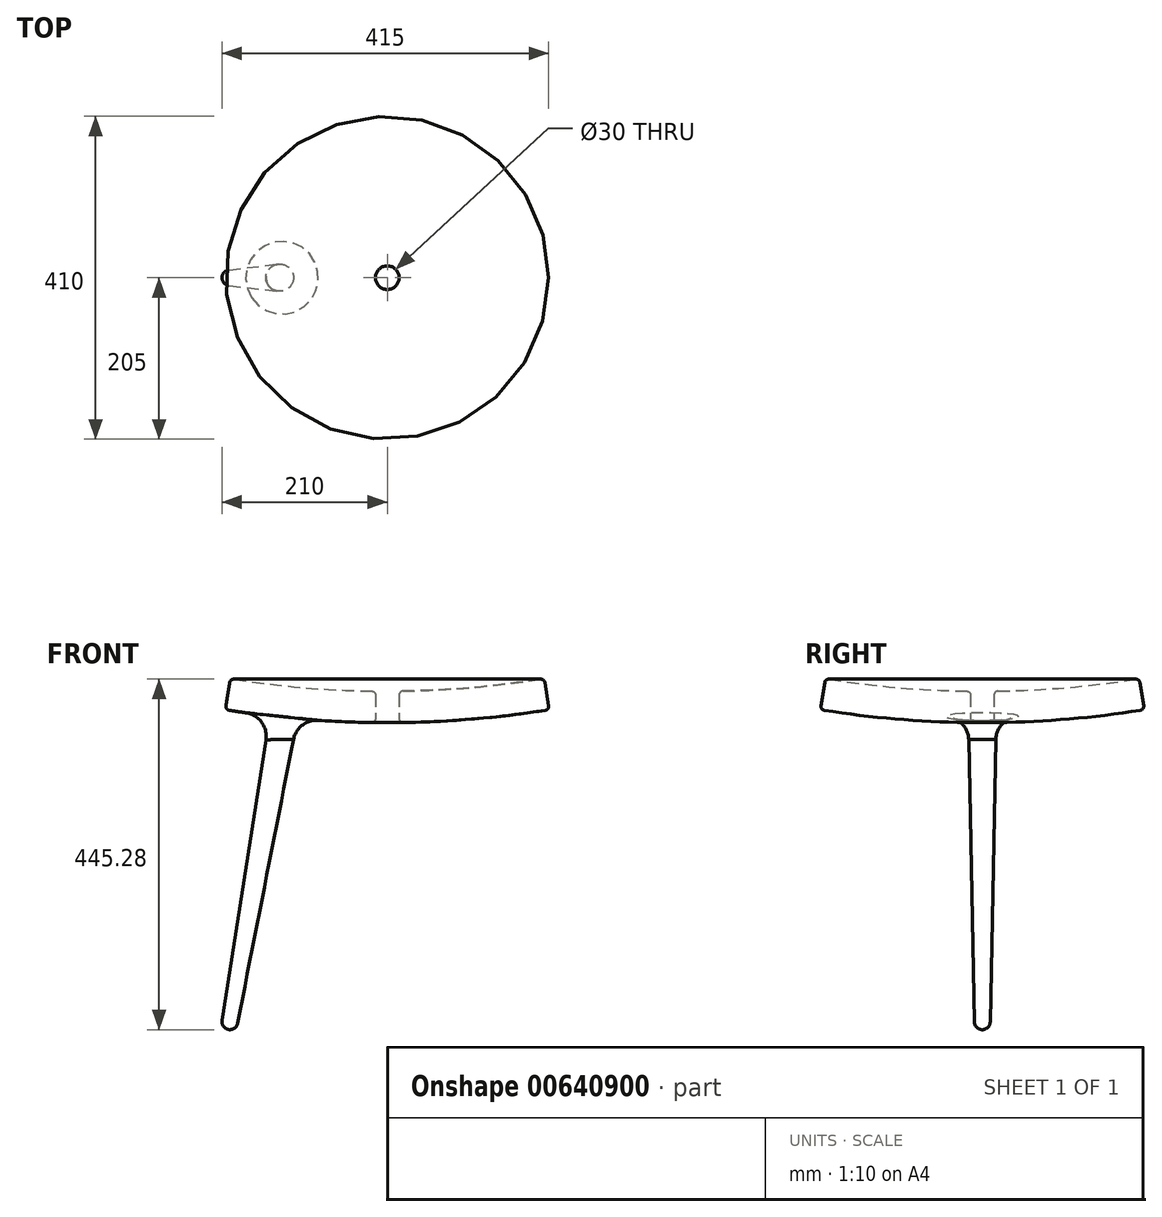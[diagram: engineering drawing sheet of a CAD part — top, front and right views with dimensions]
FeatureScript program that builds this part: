
annotation { "Feature Type Name" : "Feature", "Feature Type Description" : "" }
export const myFeature = defineFeature(function(context is Context, id is Id, definition is map)
    precondition{}
    {
        {
            var Q0;
            Q0=qCreatedBy(makeId("Front.planeOp"),FACE);
            var sketch = newSketch(context, id + "F0", { "sketchPlane" : qUnion([Q0])});
            skArc(sketch, "E0", {"start": v(0, 430) * mm, "mid": v(100, 434) * mm, "end": v(199.36, 446) * mm});
            skLineSegment(sketch, "E1", {"start": v(0, 0) * mm, "end": v(0, 1680) * mm, "construction": true});
            skLineSegment(sketch, "E2", {"start": v(199.36, 446) * mm, "end": v(205.74, 406.51) * mm});
            skArc(sketch, "E3.0", {"start": v(0, 390) * mm, "mid": v(103.2, 394.13) * mm, "end": v(205.74, 406.51) * mm});
            skLineSegment(sketch, "E4", {"start": v(0, 430) * mm, "end": v(0, 390) * mm});
            skSolve(sketch);
        }
        {
            var Q0;
            Q0=makeQuery(id+"F0.imprint","IMPRINT",FACE,{"disambiguationData":[TD([[makeQuery(id+"F0.imprint","IMPRINT",EDGE,{"derivedFrom":sQuery(id+"F0.wireOp",EDGE,"E0")}),-1.0]])]});
            var Q1;
            Q1=sQuery(id+"F0.wireOp",EDGE,"E1");
            revolve(context, id + "F1", {"entities" : qUnion([Q0]), "axis" : qUnion([Q1]), "revolveType" : RevolveType.FULL});
        }
        {
            var Q0;
            Q0=qCreatedBy(makeId("Front.planeOp"),FACE);
            var sketch = newSketch(context, id + "F2", { "sketchPlane" : qUnion([Q0])});
            skLineSegment(sketch, "E5", {"start": v(0, 0) * mm, "end": v(-318.45, 0) * mm, "construction": true});
            skArc(sketch, "E6", {"start": v(-201.74, 0.15) * mm, "mid": v(-194.35, 1.75) * mm, "end": v(-190.19, 8.07) * mm});
            skLineSegment(sketch, "E7", {"start": v(-201.74, 0.15) * mm, "end": v(-130.54, 403.92) * mm});
            skPoint(sketch, "E8.orphan", {"position": v(0, 0) * mm});
            skLineSegment(sketch, "E9", {"start": v(-130.54, 403.92) * mm, "end": v(-112.81, 400.8) * mm});
            skLineSegment(sketch, "E10", {"start": v(-112.81, 400.8) * mm, "end": v(-190.19, 8.07) * mm});
            skSolve(sketch);
        }
        {
            var Q0;
            Q0=qCreatedBy(makeId("Front.planeOp"),FACE);
            var sketch = newSketch(context, id + "F3", { "sketchPlane" : qUnion([Q0])});
            skLineSegment(sketch, "E11", {"start": v(0, 0) * mm, "end": v(0, 234.57) * mm, "construction": true});
            skSolve(sketch);
        }
        {
            var Q0;
            Q0=makeQuery(id+"F2.imprint","IMPRINT",FACE,{"disambiguationData":[TD([[makeQuery(id+"F2.imprint","IMPRINT",EDGE,{"derivedFrom":sQuery(id+"F2.wireOp",EDGE,"E6")}),1.0]])]});
            var Q1;
            Q1=sQuery(id+"F2.wireOp",EDGE,"E7");
            revolve(context, id + "F4", {"operationType" : NewBodyOperationType.ADD, "entities" : qUnion([Q0]), "axis" : qUnion([Q1]), "revolveType" : RevolveType.FULL});
        }
        {
            var Q0;
            Q0=makeQuery(id+"Fkk3XBELj9BTLDk_1.1.F4.boolean.opBoolean","INTERSECT",EDGE,{"derivedFrom":[makeQuery(id+"F1.opRevolve","SWEPT_FACE",FACE,{"disambiguationData":[OSD([sQuery(id+"F0.wireOp",EDGE,"E3.0")])]}),makeQuery(id+"Fkk3XBELj9BTLDk_1.1.F4.opRevolve","SWEPT_FACE",FACE,{"disambiguationData":[OSD([sQuery(id+"F2.wireOp",EDGE,"E10")])]})]});
            var Q1;
            Q1=makeQuery(id+"Fkk3XBELj9BTLDk_1.2.F4.boolean.opBoolean","INTERSECT",EDGE,{"derivedFrom":[makeQuery(id+"F1.opRevolve","SWEPT_FACE",FACE,{"disambiguationData":[OSD([sQuery(id+"F0.wireOp",EDGE,"E3.0")])]}),makeQuery(id+"Fkk3XBELj9BTLDk_1.2.F4.opRevolve","SWEPT_FACE",FACE,{"disambiguationData":[OSD([sQuery(id+"F2.wireOp",EDGE,"E10")])]})]});
            var Q2;
            Q2=makeQuery(id+"Fkk3XBELj9BTLDk_1.3.F4.boolean.opBoolean","INTERSECT",EDGE,{"derivedFrom":[makeQuery(id+"F1.opRevolve","SWEPT_FACE",FACE,{"disambiguationData":[OSD([sQuery(id+"F0.wireOp",EDGE,"E3.0")])]}),makeQuery(id+"Fkk3XBELj9BTLDk_1.3.F4.opRevolve","SWEPT_FACE",FACE,{"disambiguationData":[OSD([sQuery(id+"F2.wireOp",EDGE,"E10")])]})]});
            var Q3;
            Q3=makeQuery(id+"F4.boolean.opBoolean","INTERSECT",EDGE,{"derivedFrom":[makeQuery(id+"F1.opRevolve","SWEPT_FACE",FACE,{"disambiguationData":[OSD([sQuery(id+"F0.wireOp",EDGE,"E3.0")])]}),makeQuery(id+"F4.opRevolve","SWEPT_FACE",FACE,{"disambiguationData":[OSD([sQuery(id+"F2.wireOp",EDGE,"E10")])]})]});
            fillet(context, id + "F5", {"entities" : qUnion([Q0, Q1, Q2, Q3]), "radius" : 30 * mm, "tangentPropagation" : true, "allowEdgeOverflow" : false});
        }
        {
            var Q0;
            Q0=makeQuery(id+"F1.opRevolve","SWEPT_EDGE",EDGE,{"disambiguationData":[OSD([sQuery(id+"F0.wireOp",EDGE,"E0"),sQuery(id+"F0.wireOp",EDGE,"E2")])]});
            var Q1;
            Q1=makeQuery(id+"F1.opRevolve","SWEPT_EDGE",EDGE,{"disambiguationData":[OSD([sQuery(id+"F0.wireOp",EDGE,"E2"),sQuery(id+"F0.wireOp",EDGE,"E3.0")])]});
            fillet(context, id + "F6", {"entities" : qUnion([Q0, Q1]), "radius" : 5 * mm, "tangentPropagation" : true, "allowEdgeOverflow" : false});
        }
        {
            var Q0;
            Q0=qCreatedBy(makeId("Top.planeOp"),FACE);
            var sketch = newSketch(context, id + "F7", { "sketchPlane" : qUnion([Q0])});
            skCircle(sketch, "E12", {"center": v(0, 0) * mm, "radius": 15 * mm});
            skSolve(sketch);
        }
        {
            var Q0;
            Q0 = qSketchRegion(id + "F7", true);
            extrude(context, id + "F8", {"entities" : qUnion([Q0]), "operationType" : NewBodyOperationType.REMOVE, "depth" : 575 * mm, "offsetDistance" : 25 * mm});
        }
        {
            var Q0;
            Q0=makeQuery(id+"F8.boolean.opBoolean","INTERSECT",EDGE,{"derivedFrom":[makeQuery(id+"F1.opRevolve","SWEPT_FACE",FACE,{"disambiguationData":[OSD([sQuery(id+"F0.wireOp",EDGE,"E0")])]}),makeQuery(id+"F8.opExtrude","SWEPT_FACE",FACE,{"disambiguationData":[OSD([sQuery(id+"F7.wireOp",EDGE,"E12")])]})]});
            var Q1;
            Q1=makeQuery(id+"F8.boolean.opBoolean","INTERSECT",EDGE,{"derivedFrom":[makeQuery(id+"F1.opRevolve","SWEPT_FACE",FACE,{"disambiguationData":[OSD([sQuery(id+"F0.wireOp",EDGE,"E3.0")])]}),makeQuery(id+"F8.opExtrude","SWEPT_FACE",FACE,{"disambiguationData":[OSD([sQuery(id+"F7.wireOp",EDGE,"E12")])]})]});
            fillet(context, id + "F9", {"entities" : qUnion([Q0, Q1]), "radius" : 5 * mm, "tangentPropagation" : true, "allowEdgeOverflow" : false});
        }
    });
